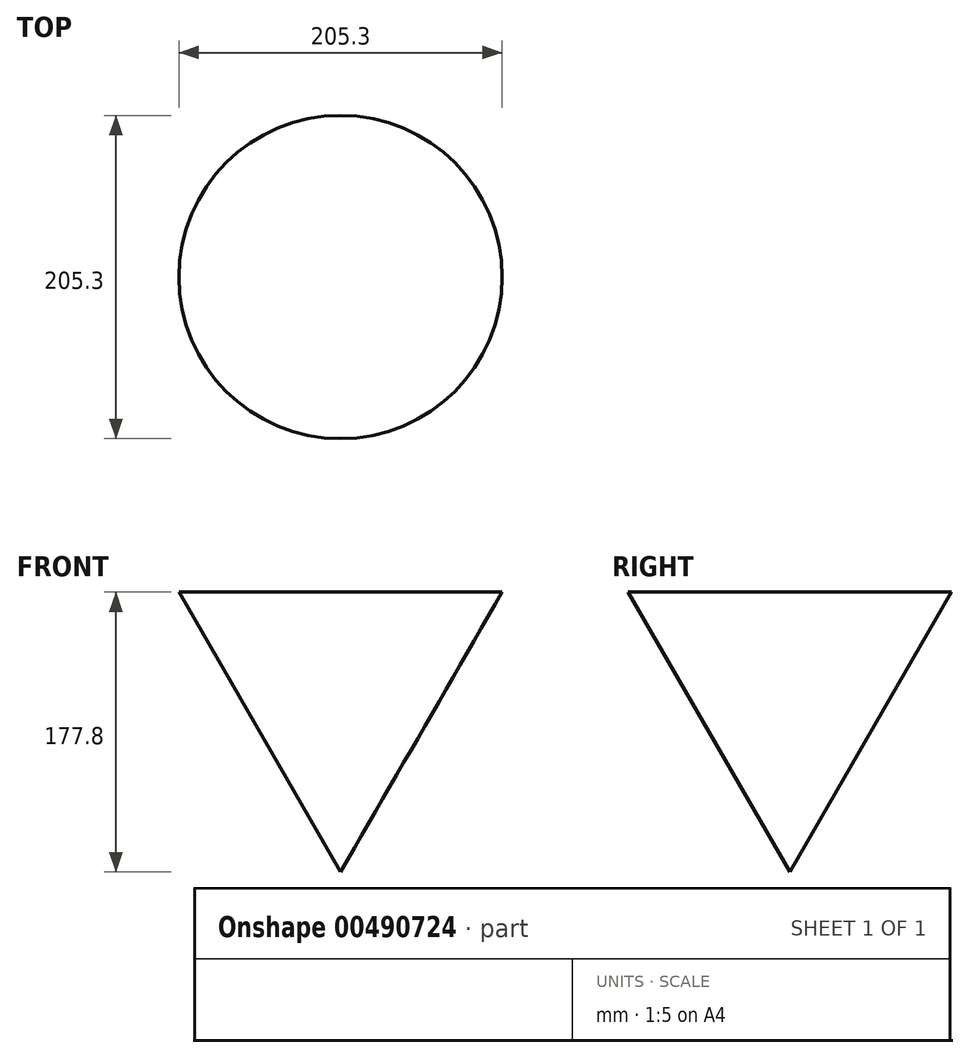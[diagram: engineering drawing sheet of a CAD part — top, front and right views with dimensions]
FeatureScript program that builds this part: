
annotation { "Feature Type Name" : "Feature", "Feature Type Description" : "" }
export const myFeature = defineFeature(function(context is Context, id is Id, definition is map)
    precondition{}
    {
        {
            var Q0;
            Q0=qCreatedBy(makeId("Front.planeOp"),FACE);
            var sketch = newSketch(context, id + "F0", { "sketchPlane" : qUnion([Q0])});
            skLineSegment(sketch, "E0", {"start": v(0, 0) * mm, "end": v(102.65, 177.8) * mm});
            skLineSegment(sketch, "E1", {"start": v(0, 0) * mm, "end": v(-102.65, 177.8) * mm});
            skLineSegment(sketch, "E2", {"start": v(0, 0) * mm, "end": v(0, 177.8) * mm});
            skLineSegment(sketch, "E3", {"start": v(102.65, 177.8) * mm, "end": v(0, 177.8) * mm});
            skLineSegment(sketch, "E4", {"start": v(0, 177.8) * mm, "end": v(-102.65, 177.8) * mm});
            skSolve(sketch);
        }
        {
            var Q0;
            Q0=makeQuery(id+"F0.imprint","IMPRINT",FACE,{"disambiguationData":[TD([[makeQuery(id+"F0.imprint","IMPRINT",EDGE,{"derivedFrom":sQuery(id+"F0.wireOp",EDGE,"E1")}),-1.0]])]});
            var Q1;
            Q1=sQuery(id+"F0.wireOp",EDGE,"E2");
            revolve(context, id + "F1", {"entities" : qUnion([Q0]), "axis" : qUnion([Q1]), "revolveType" : RevolveType.FULL});
        }
    });
